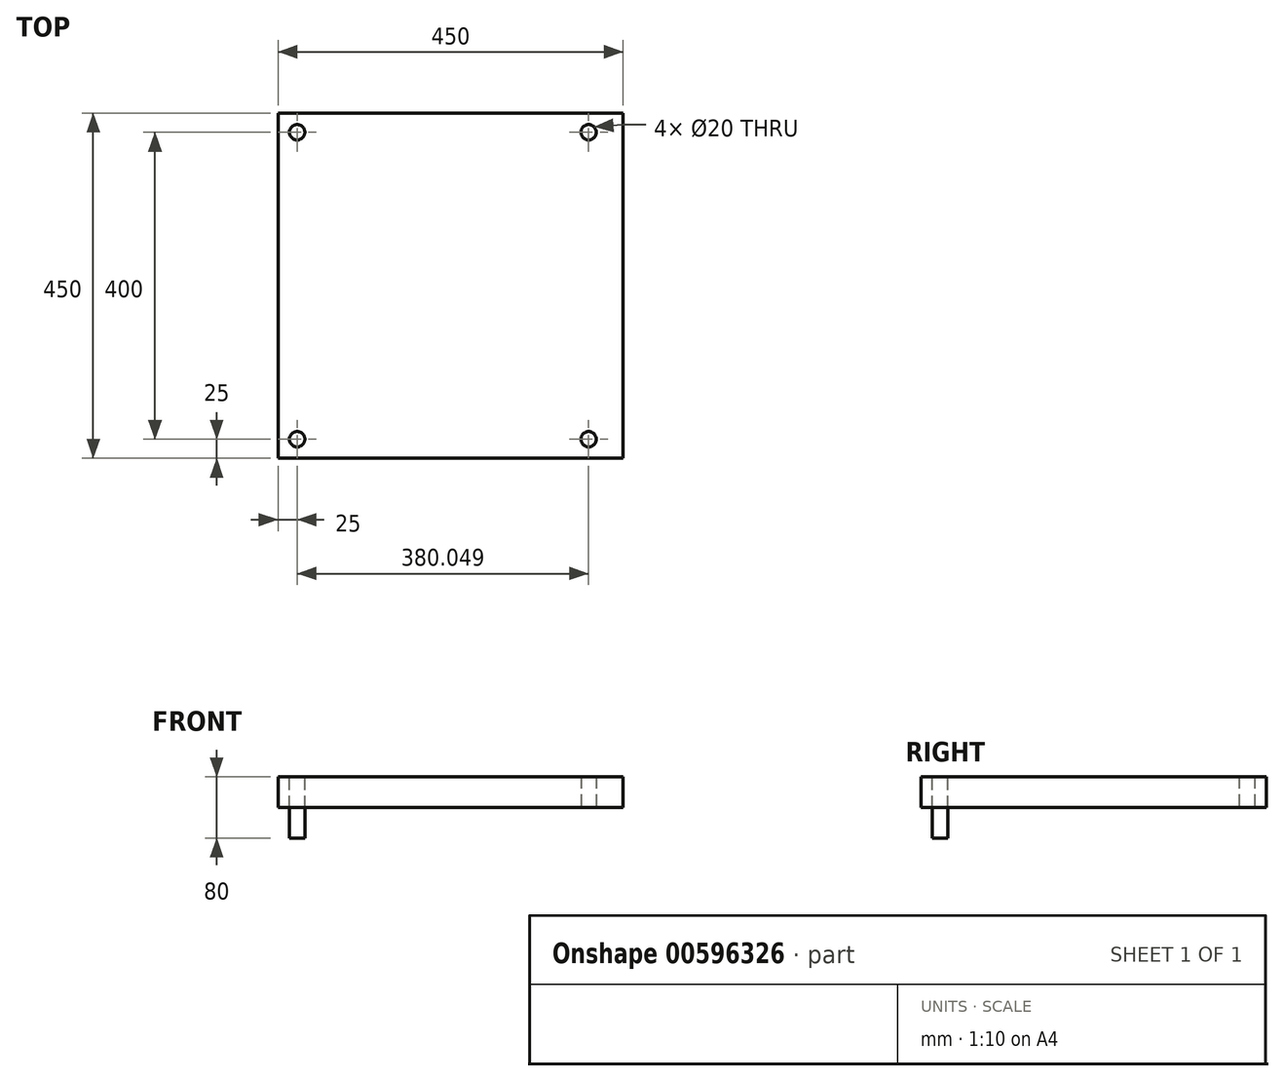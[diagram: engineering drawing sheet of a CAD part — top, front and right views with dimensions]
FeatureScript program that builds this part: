
annotation { "Feature Type Name" : "Feature", "Feature Type Description" : "" }
export const myFeature = defineFeature(function(context is Context, id is Id, definition is map)
    precondition{}
    {
        {
            var Q0;
            Q0=qCreatedBy(makeId("Top.planeOp"),FACE);
            var sketch = newSketch(context, id + "F0", { "sketchPlane" : qUnion([Q0])});
            skLineSegment(sketch, "E0.bottom", {"start": v(225, -225) * mm, "end": v(-225, -225) * mm});
            skLineSegment(sketch, "E0.top", {"start": v(225, 225) * mm, "end": v(-225, 225) * mm});
            skLineSegment(sketch, "E0.left", {"start": v(225, -225) * mm, "end": v(225, 225) * mm});
            skLineSegment(sketch, "E0.right", {"start": v(-225, -225) * mm, "end": v(-225, 225) * mm});
            skPoint(sketch, "E0.middle", {"position": v(0, 0) * mm});
            skCircle(sketch, "E1", {"center": v(-200, 200) * mm, "radius": 10 * mm});
            skCircle(sketch, "E2", {"center": v(-200, -200) * mm, "radius": 10 * mm});
            skCircle(sketch, "E3", {"center": v(180.05, -200) * mm, "radius": 10 * mm});
            skCircle(sketch, "E4", {"center": v(180.05, 200) * mm, "radius": 10 * mm});
            skSolve(sketch);
        }
        {
            var Q0;
            Q0=makeQuery(id+"F0.imprint","IMPRINT",FACE,{"disambiguationData":[TD([[makeQuery(id+"F0.imprint","IMPRINT",EDGE,{"derivedFrom":sQuery(id+"F0.wireOp",EDGE,"E0.bottom")}),-1.0]])]});
            extrude(context, id + "F1", {"entities" : qUnion([Q0]), "depth" : 40 * mm, "offsetDistance" : 25 * mm});
        }
        {
            var Q0;
            Q0=makeQuery(id+"F1.opExtrude","CAP_FACE",FACE,{"disambiguationData":[OSD([sQuery(id+"F0.wireOp",EDGE,"E0.bottom"),sQuery(id+"F0.wireOp",EDGE,"E0.top"),sQuery(id+"F0.wireOp",EDGE,"E0.left"),sQuery(id+"F0.wireOp",EDGE,"E0.right"),sQuery(id+"F0.wireOp",EDGE,"E1"),sQuery(id+"F0.wireOp",EDGE,"E2"),sQuery(id+"F0.wireOp",EDGE,"E3"),sQuery(id+"F0.wireOp",EDGE,"E4")])],"isStart":false});
            var sketch = newSketch(context, id + "F2", { "sketchPlane" : qUnion([Q0])});
            skCircle(sketch, "E5.0", {"center": v(-200, -200) * mm, "radius": 10 * mm});
            skSolve(sketch);
        }
        {
            var Q0;
            Q0 = qSketchRegion(id + "F2", true);
            extrude(context, id + "F3", {"entities" : qUnion([Q0]), "oppositeDirection" : true, "depth" : 80 * mm, "offsetDistance" : 25 * mm});
        }
        {
            var Q0;
            Q0=makeQuery(id+"F1.opExtrude","CAP_FACE",FACE,{"disambiguationData":[OSD([sQuery(id+"F0.wireOp",EDGE,"E0.bottom"),sQuery(id+"F0.wireOp",EDGE,"E0.top"),sQuery(id+"F0.wireOp",EDGE,"E0.left"),sQuery(id+"F0.wireOp",EDGE,"E0.right"),sQuery(id+"F0.wireOp",EDGE,"E1"),sQuery(id+"F0.wireOp",EDGE,"E2"),sQuery(id+"F0.wireOp",EDGE,"E3"),sQuery(id+"F0.wireOp",EDGE,"E4")])],"isStart":true});
            var sketch = newSketch(context, id + "F4", { "sketchPlane" : qUnion([Q0])});
            skCircle(sketch, "E6", {"center": v(-200, 200) * mm, "radius": 25 * mm});
            skSolve(sketch);
        }
        {
            var Q0;
            Q0=sQuery(id+"F4.wireOp",EDGE,"E6");
            extrude(context, id + "F5", {"bodyType" : ToolBodyType.SURFACE, "surfaceEntities" : qUnion([Q0]), "depth" : 420 * mm, "offsetDistance" : 25 * mm});
        }
    });
